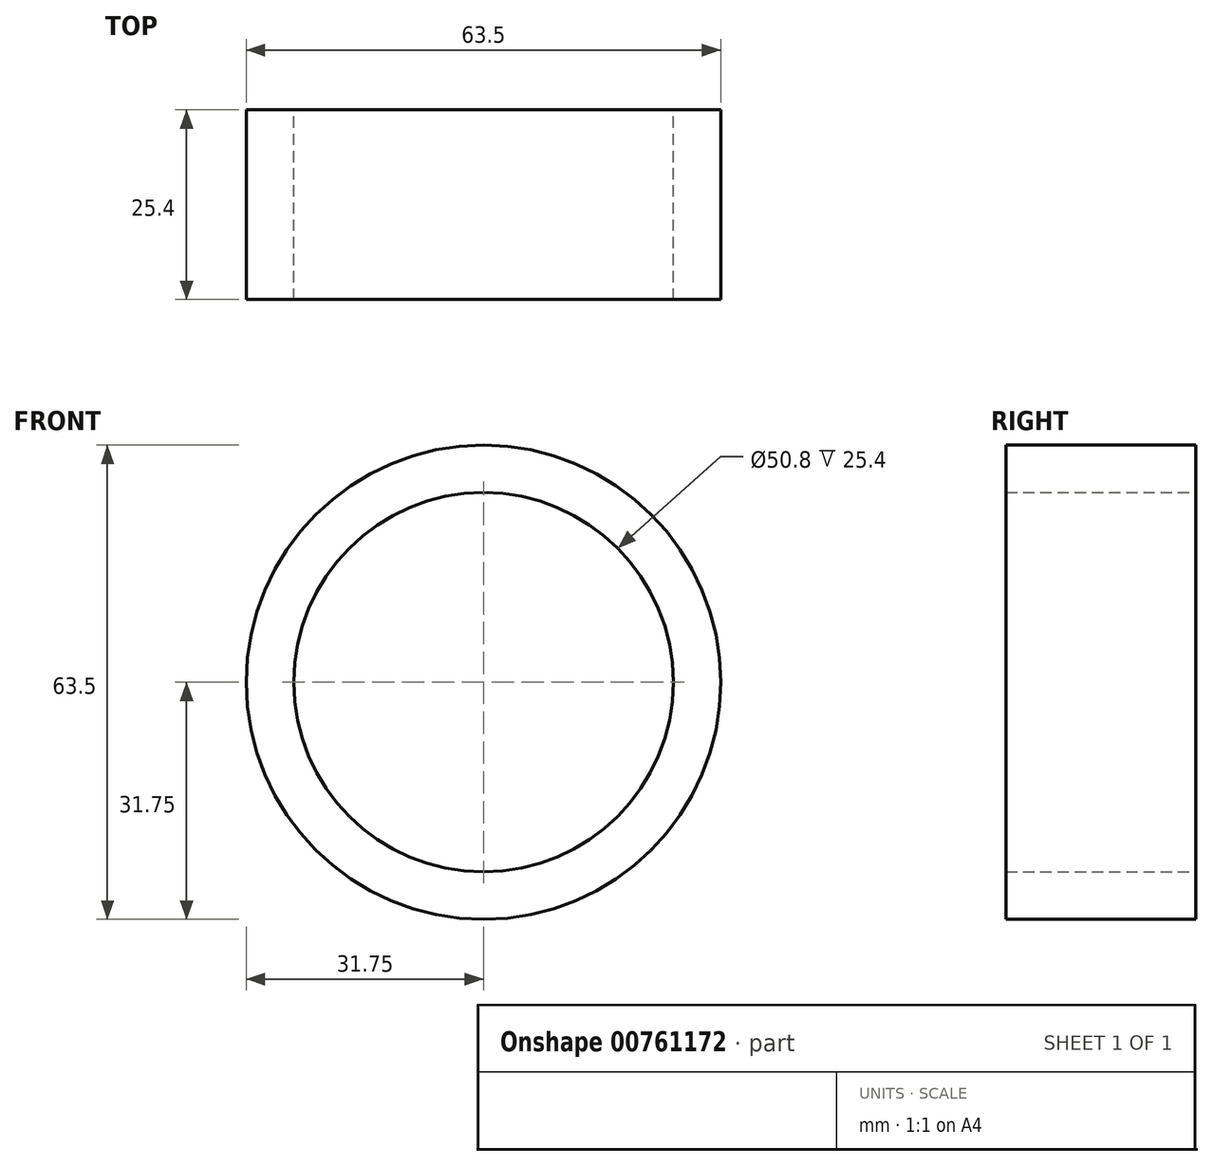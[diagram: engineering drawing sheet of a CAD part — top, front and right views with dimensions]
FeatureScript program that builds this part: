
annotation { "Feature Type Name" : "Feature", "Feature Type Description" : "" }
export const myFeature = defineFeature(function(context is Context, id is Id, definition is map)
    precondition{}
    {
        {
            var Q0;
            Q0=qCreatedBy(makeId("Front.planeOp"),FACE);
            var sketch = newSketch(context, id + "F0", { "sketchPlane" : qUnion([Q0])});
            skCircle(sketch, "E0", {"center": v(0, 0) * mm, "radius": 31.75 * mm});
            skCircle(sketch, "E1", {"center": v(0, 0) * mm, "radius": 25.4 * mm});
            skSolve(sketch);
        }
        {
            var Q0;
            Q0=makeQuery(id+"F0.imprint","IMPRINT",FACE,{"disambiguationData":[TD([[makeQuery(id+"F0.imprint","IMPRINT",EDGE,{"derivedFrom":sQuery(id+"F0.wireOp",EDGE,"E0")}),1.0]])]});
            extrude(context, id + "F1", {"entities" : qUnion([Q0]), "depth" : 25.4 * mm, "offsetDistance" : 25.4 * mm});
        }
    });
